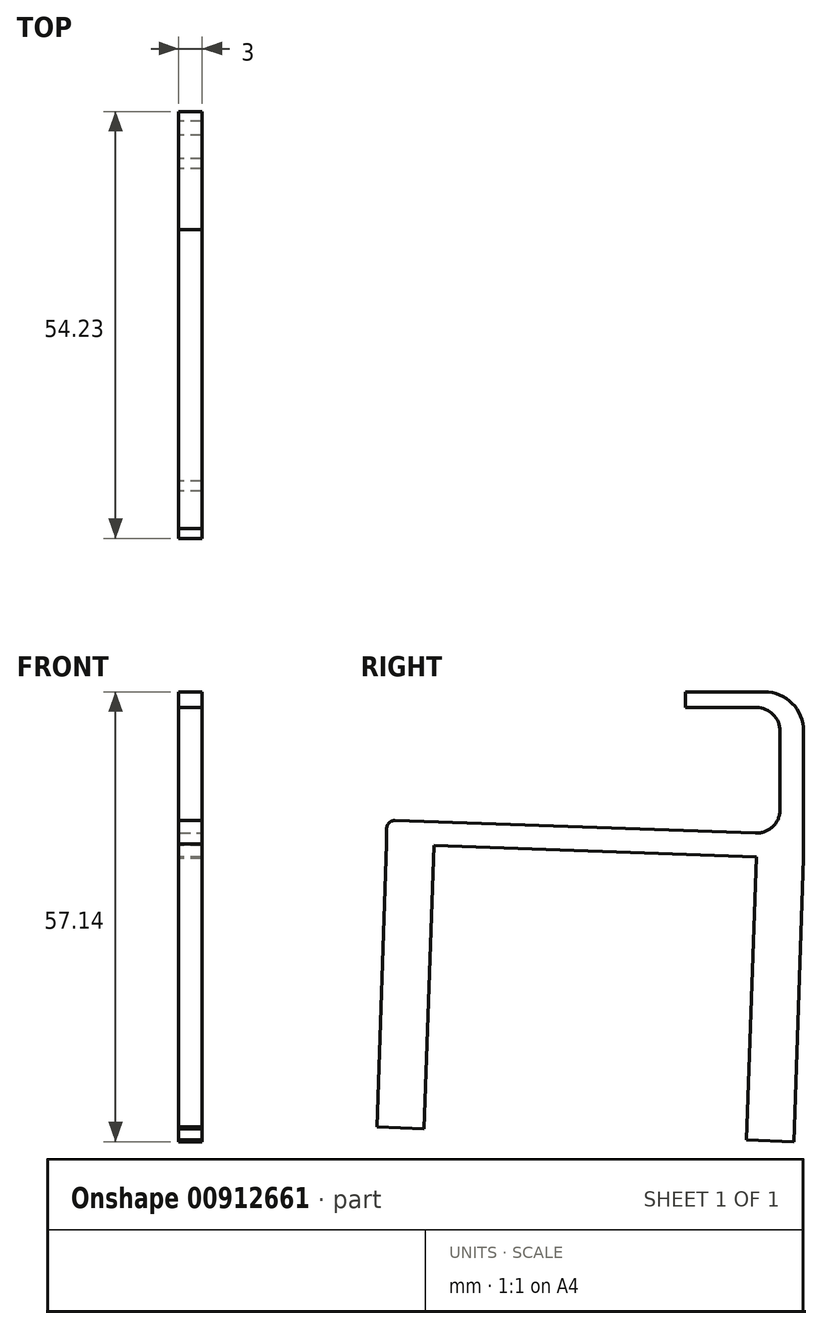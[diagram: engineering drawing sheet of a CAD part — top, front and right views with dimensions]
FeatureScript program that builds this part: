
annotation { "Feature Type Name" : "Feature", "Feature Type Description" : "" }
export const myFeature = defineFeature(function(context is Context, id is Id, definition is map)
    precondition{}
    {
        {
            var Q0;
            Q0=qCreatedBy(makeId("Right.planeOp"),FACE);
            var sketch = newSketch(context, id + "F0", { "sketchPlane" : qUnion([Q0])});
            skLineSegment(sketch, "E0", {"start": v(-3, 19.16) * mm, "end": v(-15, 19.16) * mm});
            skLineSegment(sketch, "E1", {"start": v(-15, 19.16) * mm, "end": v(-15, 21.16) * mm});
            skLineSegment(sketch, "E2", {"start": v(-15, 21.16) * mm, "end": v(0, 21.16) * mm});
            skLineSegment(sketch, "E3", {"start": v(0, 21.16) * mm, "end": v(0, 0) * mm});
            skLineSegment(sketch, "E4", {"start": v(-3, 3.1) * mm, "end": v(-3, 19.16) * mm});
            skLineSegment(sketch, "E5", {"start": v(0, 0) * mm, "end": v(-52.97, 1.85) * mm});
            skLineSegment(sketch, "E6", {"start": v(-52.97, 1.85) * mm, "end": v(-52.97, 4.85) * mm});
            skLineSegment(sketch, "E7", {"start": v(-52.97, 4.85) * mm, "end": v(-3, 3.1) * mm});
            skLineSegment(sketch, "E8", {"start": v(-52.97, 1.85) * mm, "end": v(-54.23, -34.13) * mm});
            skLineSegment(sketch, "E9", {"start": v(-54.23, -34.13) * mm, "end": v(-48.23, -34.34) * mm});
            skLineSegment(sketch, "E10", {"start": v(0, 0) * mm, "end": v(-1.26, -35.98) * mm});
            skLineSegment(sketch, "E11", {"start": v(-1.26, -35.98) * mm, "end": v(-7.25, -35.77) * mm});
            skLineSegment(sketch, "E12", {"start": v(-7.25, -35.77) * mm, "end": v(-6, 0.2) * mm});
            skLineSegment(sketch, "E13", {"start": v(-48.23, -34.34) * mm, "end": v(-46.97, 1.64) * mm});
            skSolve(sketch);
        }
        {
            var Q0;
            Q0=makeQuery(id+"F0.imprint","IMPRINT",FACE,{"disambiguationData":[TD([[makeQuery(id+"F0.imprint","IMPRINT",EDGE,{"derivedFrom":sQuery(id+"F0.wireOp",EDGE,"E0")}),-1.0]])]});
            var Q1;
            {var subQ0=sQuery(id+"F0.wireOp",EDGE,"E10");Q1=makeQuery(id+"F0.imprint","IMPRINT",FACE,{"disambiguationData":[TD([[makeQuery(id+"F0.imprint","IMPRINT",EDGE,{"derivedFrom":subQ0}),-1.0]])]});}
            var Q2;
            {var subQ0=sQuery(id+"F0.wireOp",EDGE,"E8");Q2=makeQuery(id+"F0.imprint","IMPRINT",FACE,{"disambiguationData":[TD([[makeQuery(id+"F0.imprint","IMPRINT",EDGE,{"derivedFrom":subQ0}),1.0]])]});}
            extrude(context, id + "F1", {"entities" : qUnion([Q0, Q1, Q2]), "endBound" : BoundingType.SYMMETRIC, "depth" : 3 * mm, "offsetDistance" : 25 * mm});
        }
        {
            var Q0;
            Q0=makeQuery(id+"F1.opExtrude","SWEPT_EDGE",EDGE,{"disambiguationData":[OSD([sQuery(id+"F0.wireOp",EDGE,"E0"),sQuery(id+"F0.wireOp",EDGE,"E4")])]});
            var Q1;
            Q1=makeQuery(id+"F1.opExtrude","SWEPT_EDGE",EDGE,{"disambiguationData":[OSD([sQuery(id+"F0.wireOp",EDGE,"E4"),sQuery(id+"F0.wireOp",EDGE,"E7")])]});
            fillet(context, id + "F2", {"entities" : qUnion([Q0, Q1]), "radius" : 3 * mm, "tangentPropagation" : true, "allowEdgeOverflow" : false});
        }
        {
            var Q0;
            Q0=makeQuery(id+"F1.opExtrude","SWEPT_EDGE",EDGE,{"disambiguationData":[OSD([sQuery(id+"F0.wireOp",EDGE,"E6"),sQuery(id+"F0.wireOp",EDGE,"E7")])]});
            fillet(context, id + "F3", {"entities" : qUnion([Q0]), "radius" : 1 * mm, "tangentPropagation" : true, "allowEdgeOverflow" : false});
        }
        {
            var Q0;
            Q0=makeQuery(id+"F1.opExtrude","SWEPT_EDGE",EDGE,{"disambiguationData":[OSD([sQuery(id+"F0.wireOp",EDGE,"E2"),sQuery(id+"F0.wireOp",EDGE,"E3")])]});
            fillet(context, id + "F4", {"entities" : qUnion([Q0]), "radius" : 5 * mm, "tangentPropagation" : true, "allowEdgeOverflow" : false});
        }
    });
